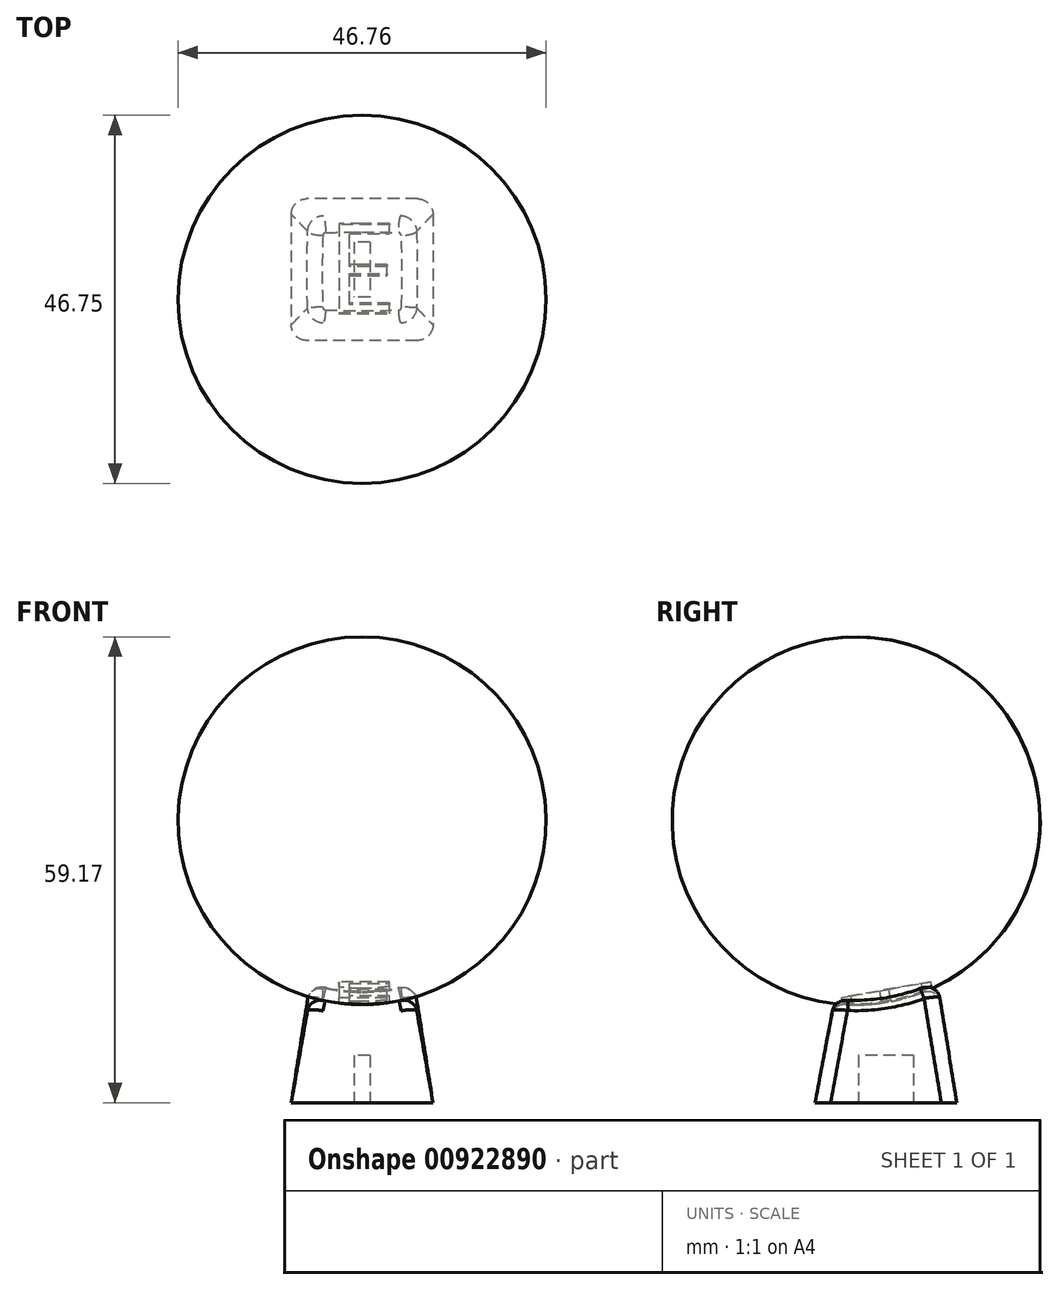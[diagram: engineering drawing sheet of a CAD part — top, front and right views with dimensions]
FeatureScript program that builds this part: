
annotation { "Feature Type Name" : "Feature", "Feature Type Description" : "" }
export const myFeature = defineFeature(function(context is Context, id is Id, definition is map)
    precondition{}
    {
        {
            var Q0;
            Q0=qCreatedBy(makeId("Top.planeOp"),FACE);
            var sketch = newSketch(context, id + "F0", { "sketchPlane" : qUnion([Q0])});
            skLineSegment(sketch, "E0.bottom", {"start": v(9, 9) * mm, "end": v(-9, 9) * mm});
            skLineSegment(sketch, "E0.top", {"start": v(9, -9) * mm, "end": v(-9, -9) * mm});
            skLineSegment(sketch, "E0.left", {"start": v(9, 9) * mm, "end": v(9, -9) * mm});
            skLineSegment(sketch, "E0.right", {"start": v(-9, 9) * mm, "end": v(-9, -9) * mm});
            skPoint(sketch, "E0.middle", {"position": v(0, 0) * mm});
            skLineSegment(sketch, "E1.bottom", {"start": v(1, 3.5) * mm, "end": v(-1, 3.5) * mm, "construction": true});
            skLineSegment(sketch, "E1.top", {"start": v(1, -3.5) * mm, "end": v(-1, -3.5) * mm, "construction": true});
            skLineSegment(sketch, "E1.left", {"start": v(1, 3.5) * mm, "end": v(1, -3.5) * mm, "construction": true});
            skLineSegment(sketch, "E1.right", {"start": v(-1, 3.5) * mm, "end": v(-1, -3.5) * mm, "construction": true});
            skSolve(sketch);
        }
        {
            var Q0;
            Q0=qCreatedBy(makeId("Right.planeOp"),FACE);
            var sketch = newSketch(context, id + "F1", { "sketchPlane" : qUnion([Q0])});
            skLineSegment(sketch, "E2.0.1", {"start": v(-9, 0) * mm, "end": v(9, 0) * mm});
            skLineSegment(sketch, "E2.0.3", {"start": v(9, 0) * mm, "end": v(-9, 0) * mm});
            skLineSegment(sketch, "E3", {"start": v(9, 0) * mm, "end": v(6.5, 15.5) * mm});
            skLineSegment(sketch, "E4", {"start": v(6.5, 15.5) * mm, "end": v(-6.5, 13.2) * mm});
            skLineSegment(sketch, "E5", {"start": v(-6.5, 13.2) * mm, "end": v(-9, 0) * mm});
            skLineSegment(sketch, "E6", {"start": v(6.5, 5.24) * mm, "end": v(-6.5, 5.24) * mm, "construction": true});
            skSolve(sketch);
        }
        {
            var Q0;
            Q0=sQuery(id+"F1.wireOp",EDGE,"E4");
            cPlane(context, id + "F2", {"entities" : qUnion([Q0]), "cplaneType" : CPlaneType.LINE_ANGLE, "offset" : 25 * mm, "angle" : 0 * degree, "oppositeDirection" : true, "width" : 150 * mm, "height" : 150 * mm});
        }
        {
            var Q0;
            Q0=qCreatedBy(id+"F2.planeOp",FACE);
            var sketch = newSketch(context, id + "F3", { "sketchPlane" : qUnion([Q0])});
            skLineSegment(sketch, "E7.0", {"start": v(0, -9.1) * mm, "end": v(0, 4.1) * mm, "construction": true});
            skLineSegment(sketch, "E8.bottom", {"start": v(6.6, 4.1) * mm, "end": v(-6.6, 4.1) * mm});
            skLineSegment(sketch, "E8.top", {"start": v(6.6, -9.1) * mm, "end": v(-6.6, -9.1) * mm});
            skLineSegment(sketch, "E8.left", {"start": v(6.6, 4.1) * mm, "end": v(6.6, -9.1) * mm});
            skLineSegment(sketch, "E8.right", {"start": v(-6.6, 4.1) * mm, "end": v(-6.6, -9.1) * mm});
            skPoint(sketch, "E8.middle", {"position": v(0, -2.5) * mm});
            skSolve(sketch);
        }
        {
            var Q0;
            Q0=qCreatedBy(id+"F2.planeOp",FACE);
            var sketch = newSketch(context, id + "F4", { "sketchPlane" : qUnion([Q0])});
            skText(sketch, "E9", { "text": "E", "fontName": "OpenSans-Regular.ttf"});
            skLineSegment(sketch, "E10", {"start": v(0, -2.5) * mm, "end": v(-9.07, -2.5) * mm, "construction": true});
            const initialGuessF4  = {"E9": [-0.00452, -0.0083, 1, 0, 0.0116]};
            skSetInitialGuess(sketch, initialGuessF4);
            skSolve(sketch);
        }
        {
            var Q0;
            Q0=makeQuery(id+"F0.imprint","IMPRINT",FACE,{"disambiguationData":[TD([[makeQuery(id+"F0.imprint","IMPRINT",EDGE,{"derivedFrom":sQuery(id+"F0.wireOp",EDGE,"E0.bottom")}),1.0]])]});
            var Q1;
            Q1=makeQuery(id+"F3.imprint","IMPRINT",FACE,{"disambiguationData":[TD([[makeQuery(id+"F3.imprint","IMPRINT",EDGE,{"derivedFrom":sQuery(id+"F3.wireOp",EDGE,"E8.bottom")}),1.0]])]});
            loft(context, id + "F5", {"sheetProfilesArray" : [{ "sheetProfileEntities" : qUnion([Q0]) }, { "sheetProfileEntities" : qUnion([Q1]) }]});
        }
        {
            var Q0;
            Q0=makeQuery(id+"F0.imprint","IMPRINT",FACE,{"disambiguationData":[TD([[makeQuery(id+"F0.imprint","IMPRINT",EDGE,{"derivedFrom":sQuery(id+"F0.wireOp",EDGE,"E0.bottom")}),1.0]])]});
            var sketch = newSketch(context, id + "F6", { "sketchPlane" : qUnion([Q0])});
            skLineSegment(sketch, "E11.0", {"start": v(1, 3.5) * mm, "end": v(1, -3.5) * mm});
            skLineSegment(sketch, "E11.1", {"start": v(1, -3.5) * mm, "end": v(-1, -3.5) * mm});
            skLineSegment(sketch, "E11.2", {"start": v(-1, 3.5) * mm, "end": v(-1, -3.5) * mm});
            skLineSegment(sketch, "E11.3", {"start": v(1, 3.5) * mm, "end": v(-1, 3.5) * mm});
            skSolve(sketch);
        }
        {
            var Q0;
            Q0=makeQuery(id+"F6.imprint","IMPRINT",FACE,{"disambiguationData":[TD([[makeQuery(id+"F6.imprint","IMPRINT",EDGE,{"derivedFrom":sQuery(id+"F6.wireOp",EDGE,"E11.0")}),-1.0]])]});
            extrude(context, id + "F7", {"entities" : qUnion([Q0]), "operationType" : NewBodyOperationType.REMOVE, "depth" : 6 * mm, "offsetDistance" : 25 * mm});
        }
        {
            var Q0;
            Q0=makeQuery(id+"F5.opLoft","SWEPT_EDGE",EDGE,{"disambiguationData":[OSD([sQuery(id+"F0.wireOp",EDGE,"E0.top"),sQuery(id+"F0.wireOp",EDGE,"E0.right"),sQuery(id+"F3.wireOp",EDGE,"E8.bottom"),sQuery(id+"F3.wireOp",EDGE,"E8.right")])]});
            var Q1;
            Q1=makeQuery(id+"F5.opLoft","SWEPT_EDGE",EDGE,{"disambiguationData":[OSD([sQuery(id+"F0.wireOp",EDGE,"E0.bottom"),sQuery(id+"F0.wireOp",EDGE,"E0.right"),sQuery(id+"F3.wireOp",EDGE,"E8.top"),sQuery(id+"F3.wireOp",EDGE,"E8.right")])]});
            var Q2;
            Q2=makeQuery(id+"F5.opLoft","SWEPT_EDGE",EDGE,{"disambiguationData":[OSD([sQuery(id+"F0.wireOp",EDGE,"E0.top"),sQuery(id+"F0.wireOp",EDGE,"E0.left"),sQuery(id+"F3.wireOp",EDGE,"E8.bottom"),sQuery(id+"F3.wireOp",EDGE,"E8.left")])]});
            var Q3;
            Q3=makeQuery(id+"F5.opLoft","SWEPT_EDGE",EDGE,{"disambiguationData":[OSD([sQuery(id+"F0.wireOp",EDGE,"E0.bottom"),sQuery(id+"F0.wireOp",EDGE,"E0.left"),sQuery(id+"F3.wireOp",EDGE,"E8.top"),sQuery(id+"F3.wireOp",EDGE,"E8.left")])]});
            fillet(context, id + "F8", {"entities" : qUnion([Q0, Q1, Q2, Q3]), "radius" : 2 * mm, "tangentPropagation" : true, "allowEdgeOverflow" : false});
        }
        {
            var Q0;
            Q0=makeQuery(id+"F5.opLoft","CAP_FACE",FACE,{"disambiguationData":[OSD([makeQuery(id+"F3.imprint","IMPRINT",FACE,{"disambiguationData":[TD([[makeQuery(id+"F3.imprint","IMPRINT",EDGE,{"derivedFrom":sQuery(id+"F3.wireOp",EDGE,"E8.bottom")}),1.0]])]})])],"isStart":true});
            var sketch = newSketch(context, id + "F9", { "sketchPlane" : qUnion([Q0])});
            skCircle(sketch, "E12", {"center": v(0, 2.5) * mm, "radius": 8.5 * mm});
            skLineSegment(sketch, "E13", {"start": v(0, 2.5) * mm, "end": v(6.6, 2.5) * mm, "construction": true});
            skLineSegment(sketch, "E14", {"start": v(0, 2.5) * mm, "end": v(0, -4.1) * mm, "construction": true});
            skSolve(sketch);
        }
        {
            var Q0;
            Q0=qCreatedBy(makeId("Right.planeOp"),FACE);
            var sketch = newSketch(context, id + "F10", { "sketchPlane" : qUnion([Q0])});
            skLineSegment(sketch, "E15.0", {"start": v(-8.37, 12.88) * mm, "end": v(8.37, 15.83) * mm, "construction": true});
            skLineSegment(sketch, "E16", {"start": v(-8.19, 60.79) * mm, "end": v(0.62, 10.8) * mm});
            skCircle(sketch, "E17", {"center": v(-3.78, 35.8) * mm, "radius": 23.38 * mm});
            skCircle(sketch, "E18", {"center": v(-3.78, 35.8) * mm, "radius": 25.38 * mm});
            skSolve(sketch);
        }
        {
            var Q0;
            {var subQ0=sQuery(id+"F10.wireOp",EDGE,"E17");var subQ1=sQuery(id+"F10.wireOp",EDGE,"E16");var subQ2=makeQuery(id+"F10.imprint","INTERSECT",VERTEX,{"disambiguationData":[OD(0.0)],"derivedFrom":[subQ1,subQ0]});Q0=makeQuery(id+"F10.imprint","IMPRINT",FACE,{"disambiguationData":[TD([[makeQuery(id+"F10.imprint","IMPRINT",EDGE,{"disambiguationData":[TD([[subQ2,-1.0]])],"derivedFrom":subQ1}),-1.0]])]});}
            var Q1;
            Q1=sQuery(id+"F10.wireOp",EDGE,"E16");
            revolve(context, id + "F11", {"operationType" : NewBodyOperationType.REMOVE, "surfaceOperationType" : NewSurfaceOperationType.NEW, "entities" : qUnion([Q0]), "axis" : qUnion([Q1]), "revolveType" : RevolveType.FULL, "oppositeDirection" : true});
        }
        {
            var Q0;
            {var subQ0=sQuery(id+"F10.wireOp",EDGE,"E18");var subQ1=sQuery(id+"F10.wireOp",EDGE,"E16");var subQ2=makeQuery(id+"F10.imprint","INTERSECT",VERTEX,{"disambiguationData":[OD(0.0)],"derivedFrom":[subQ1,subQ0]});Q0=makeQuery(id+"F10.imprint","IMPRINT",FACE,{"disambiguationData":[TD([[makeQuery(id+"F10.imprint","IMPRINT",EDGE,{"disambiguationData":[TD([[subQ2,-1.0]])],"derivedFrom":subQ1}),-1.0]])]});}
            var Q1;
            {var subQ0=sQuery(id+"F10.wireOp",EDGE,"E17");var subQ1=sQuery(id+"F10.wireOp",EDGE,"E16");var subQ2=makeQuery(id+"F10.imprint","INTERSECT",VERTEX,{"disambiguationData":[OD(0.0)],"derivedFrom":[subQ1,subQ0]});Q1=makeQuery(id+"F10.imprint","IMPRINT",FACE,{"disambiguationData":[TD([[makeQuery(id+"F10.imprint","IMPRINT",EDGE,{"disambiguationData":[TD([[subQ2,-1.0]])],"derivedFrom":subQ1}),-1.0]])]});}
            var Q2;
            Q2=sQuery(id+"F10.wireOp",EDGE,"E16");
            revolve(context, id + "F12", {"surfaceOperationType" : NewSurfaceOperationType.NEW, "entities" : qUnion([Q0, Q1]), "axis" : qUnion([Q2]), "revolveType" : RevolveType.FULL});
        }
        {
            var Q0;
            Q0=makeQuery(id+"F4.imprint","IMPRINT",FACE,{"disambiguationData":[TD([[makeQuery(id+"F4.imprint","IMPRINT",EDGE,{"derivedFrom":sQuery(id+"F4.wireOp",EDGE,"E9.sketch_text.stroke-0")}),-1.0]])]});
            var Q1;
            Q1=makeQuery(id+"F12.opRevolve","SWEPT_BODY",BODY,{"disambiguationData":[OSD([sQuery(id+"F10.wireOp",EDGE,"E16"),sQuery(id+"F10.wireOp",EDGE,"E18")])]});
            extrude(context, id + "F13", {"entities" : qUnion([Q0]), "operationType" : NewBodyOperationType.REMOVE, "endBound" : BoundingType.UP_TO_BODY, "depth" : 25 * mm, "endBoundEntityBody" : qUnion([Q1]), "offsetDistance" : 25 * mm});
        }
        {
            var Q0;
            Q0=makeQuery(id+"F11.boolean.opBoolean","INTERSECT",EDGE,{"derivedFrom":[makeQuery(id+"F5.opLoft","SWEPT_FACE",FACE,{"disambiguationData":[OSD([sQuery(id+"F0.wireOp",EDGE,"E0.bottom"),sQuery(id+"F0.wireOp",EDGE,"E0.top"),sQuery(id+"F0.wireOp",EDGE,"E0.right"),sQuery(id+"F3.wireOp",EDGE,"E8.bottom"),sQuery(id+"F3.wireOp",EDGE,"E8.top"),sQuery(id+"F3.wireOp",EDGE,"E8.right")])]}),makeQuery(id+"F11.opRevolve","SWEPT_FACE",FACE,{"disambiguationData":[OSD([sQuery(id+"F10.wireOp",EDGE,"E17")])]})]});
            var Q1;
            Q1=makeQuery(id+"F11.boolean.opBoolean","INTERSECT",EDGE,{"derivedFrom":[makeQuery(id+"F5.opLoft","SWEPT_FACE",FACE,{"disambiguationData":[OSD([sQuery(id+"F0.wireOp",EDGE,"E0.bottom"),sQuery(id+"F0.wireOp",EDGE,"E0.top"),sQuery(id+"F0.wireOp",EDGE,"E0.left"),sQuery(id+"F3.wireOp",EDGE,"E8.bottom"),sQuery(id+"F3.wireOp",EDGE,"E8.top"),sQuery(id+"F3.wireOp",EDGE,"E8.left")])]}),makeQuery(id+"F11.opRevolve","SWEPT_FACE",FACE,{"disambiguationData":[OSD([sQuery(id+"F10.wireOp",EDGE,"E17")])]})]});
            fillet(context, id + "F14", {"entities" : qUnion([Q0, Q1]), "radius" : 1.6 * mm, "tangentPropagation" : true, "allowEdgeOverflow" : false});
        }
    });
